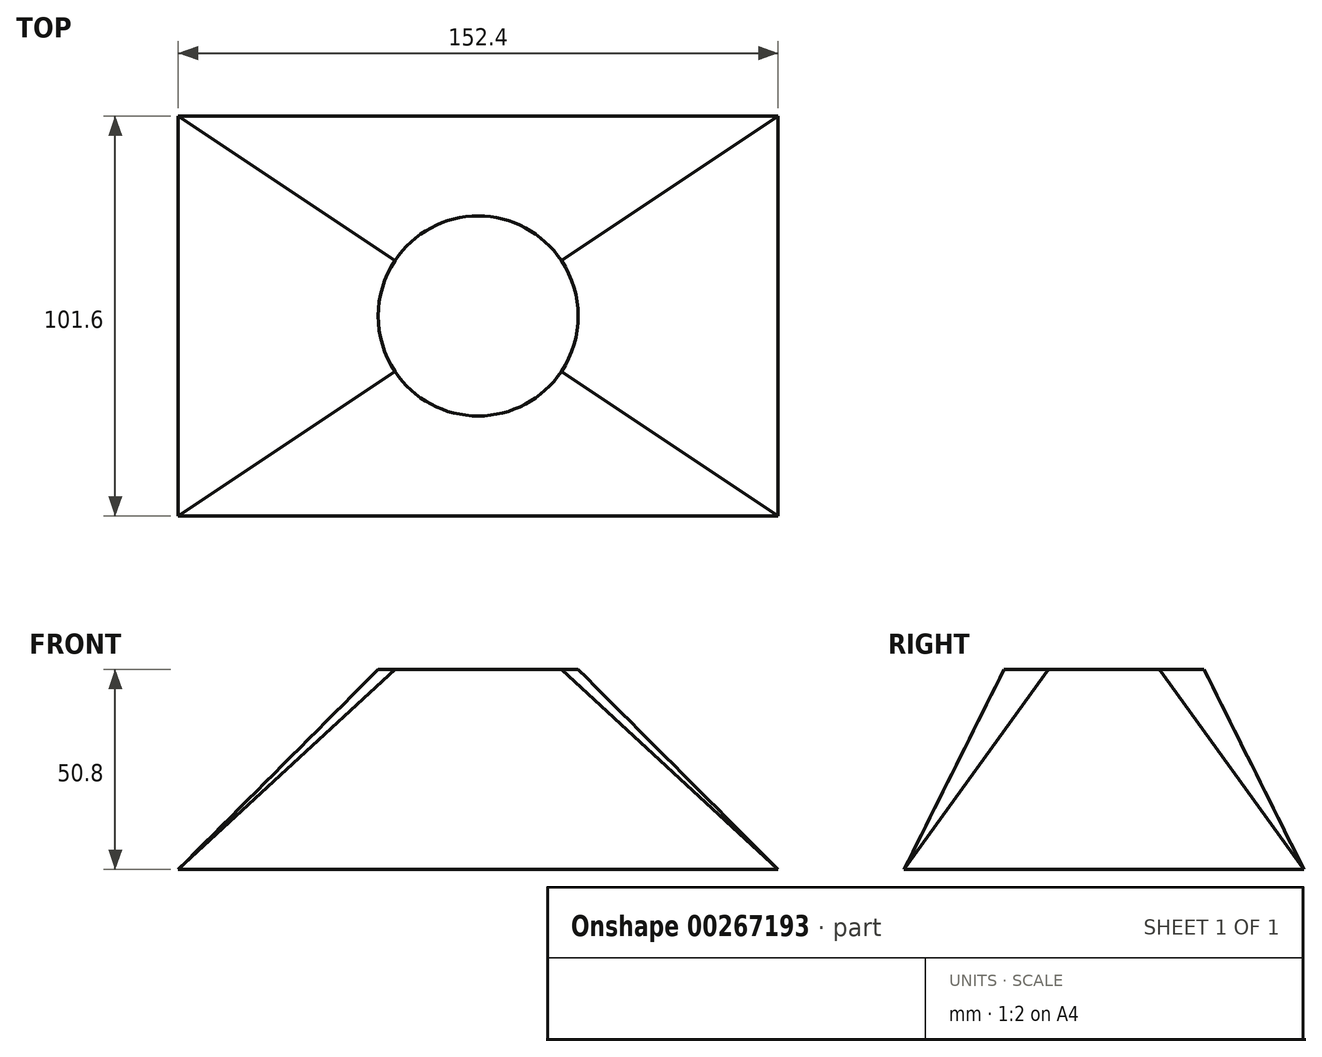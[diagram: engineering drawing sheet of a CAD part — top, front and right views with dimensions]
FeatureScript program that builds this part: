
annotation { "Feature Type Name" : "Feature", "Feature Type Description" : "" }
export const myFeature = defineFeature(function(context is Context, id is Id, definition is map)
    precondition{}
    {
        {
            var Q0;
            Q0=qCreatedBy(makeId("Top.planeOp"),FACE);
            var sketch = newSketch(context, id + "F0", { "sketchPlane" : qUnion([Q0])});
            skLineSegment(sketch, "E0.bottom", {"start": v(76.2, -50.8) * mm, "end": v(-76.2, -50.8) * mm});
            skLineSegment(sketch, "E0.top", {"start": v(76.2, 50.8) * mm, "end": v(-76.2, 50.8) * mm});
            skLineSegment(sketch, "E0.left", {"start": v(76.2, -50.8) * mm, "end": v(76.2, 50.8) * mm});
            skLineSegment(sketch, "E0.right", {"start": v(-76.2, -50.8) * mm, "end": v(-76.2, 50.8) * mm});
            skPoint(sketch, "E0.middle", {"position": v(0, 0) * mm});
            skSolve(sketch);
        }
        {
            var Q0;
            Q0=qCreatedBy(makeId("Top.planeOp"),FACE);
            cPlane(context, id + "F1", {"entities" : qUnion([Q0]), "cplaneType" : CPlaneType.OFFSET, "offset" : 50.8 * mm, "width" : 152.4 * mm, "height" : 152.4 * mm});
        }
        {
            var Q0;
            Q0=qCreatedBy(id+"F1.planeOp",FACE);
            var sketch = newSketch(context, id + "F2", { "sketchPlane" : qUnion([Q0])});
            skPoint(sketch, "E1.0", {"position": v(76.2, 50.8) * mm});
            skPoint(sketch, "E1.1", {"position": v(-76.2, 50.8) * mm});
            skPoint(sketch, "E1.2", {"position": v(-76.2, -50.8) * mm});
            skPoint(sketch, "E1.3", {"position": v(76.2, -50.8) * mm});
            skLineSegment(sketch, "E2", {"start": v(-76.2, -50.8) * mm, "end": v(76.2, 50.8) * mm, "construction": true});
            skLineSegment(sketch, "E3", {"start": v(76.2, -50.8) * mm, "end": v(-76.2, 50.8) * mm, "construction": true});
            skArc(sketch, "E4", {"start": v(21.13, 14.09) * mm, "mid": v(0, 25.4) * mm, "end": v(-21.13, 14.09) * mm});
            skArc(sketch, "E5", {"start": v(-21.13, 14.09) * mm, "mid": v(-25.4, 0) * mm, "end": v(-21.13, -14.09) * mm});
            skArc(sketch, "E6", {"start": v(-21.13, -14.09) * mm, "mid": v(0, -25.4) * mm, "end": v(21.13, -14.09) * mm});
            skArc(sketch, "E7", {"start": v(21.13, -14.09) * mm, "mid": v(25.4, 0) * mm, "end": v(21.13, 14.09) * mm});
            skSolve(sketch);
        }
        {
            var Q0;
            Q0=makeQuery(id+"F0.imprint","IMPRINT",FACE,{"disambiguationData":[TD([[makeQuery(id+"F0.imprint","IMPRINT",EDGE,{"derivedFrom":sQuery(id+"F0.wireOp",EDGE,"E0.bottom")}),-1.0]])]});
            var Q1;
            Q1=makeQuery(id+"F2.imprint","IMPRINT",FACE,{"disambiguationData":[TD([[makeQuery(id+"F2.imprint","IMPRINT",EDGE,{"derivedFrom":sQuery(id+"F2.wireOp",EDGE,"E4")}),1.0]])]});
            loft(context, id + "F3", {"sheetProfilesArray" : [{ "sheetProfileEntities" : qUnion([Q0]) }, { "sheetProfileEntities" : qUnion([Q1]) }]});
        }
    });
